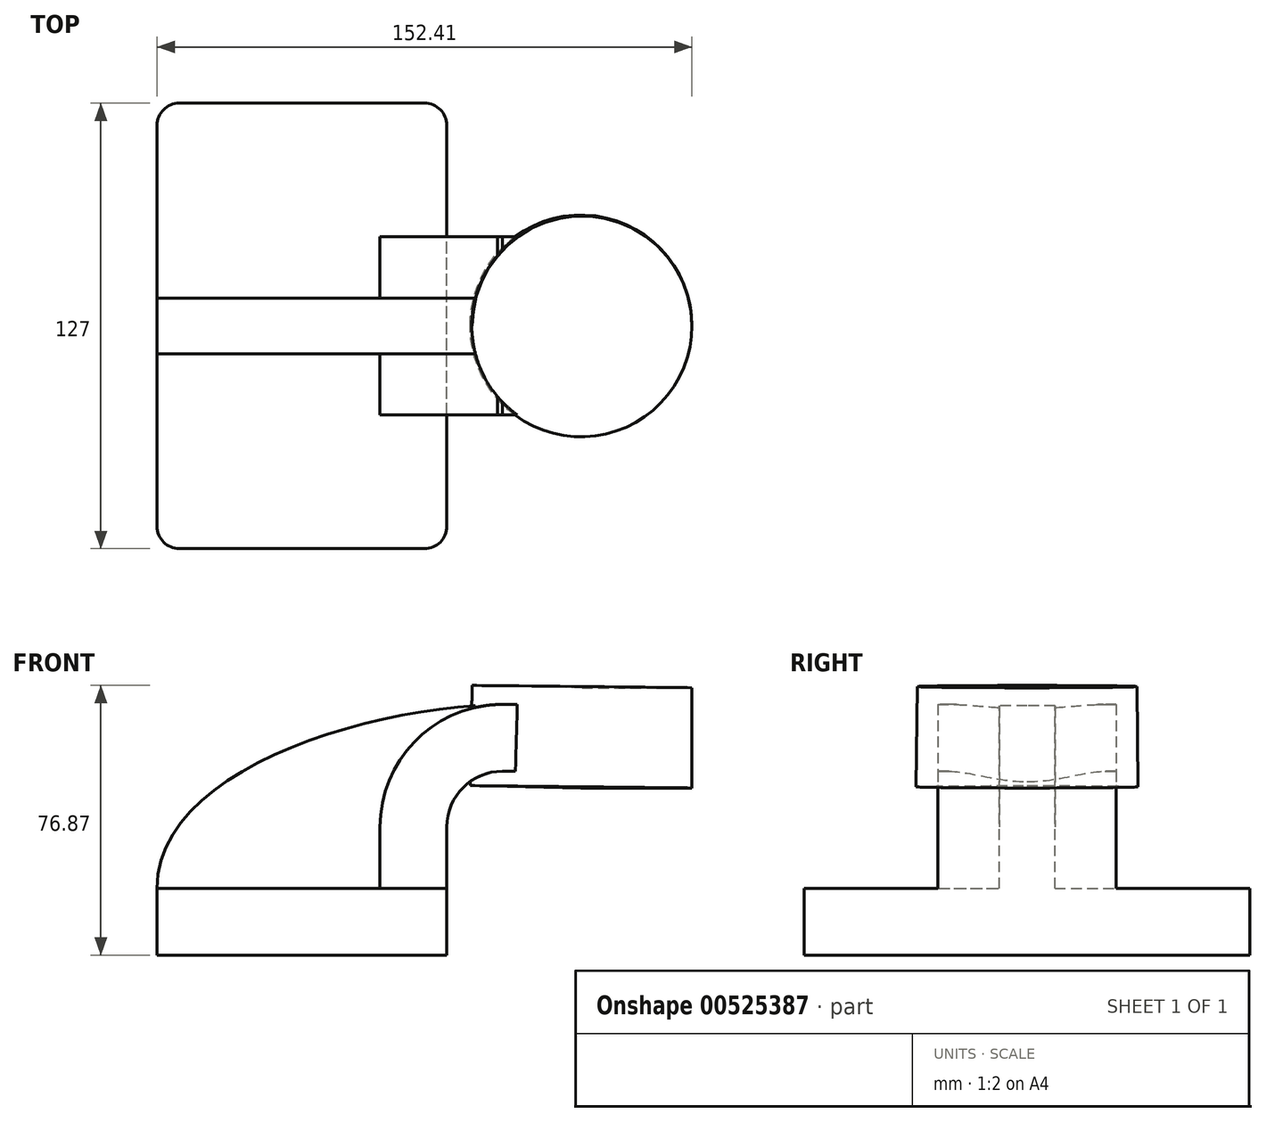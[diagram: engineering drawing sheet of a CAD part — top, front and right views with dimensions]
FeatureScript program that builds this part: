
annotation { "Feature Type Name" : "Feature", "Feature Type Description" : "" }
export const myFeature = defineFeature(function(context is Context, id is Id, definition is map)
    precondition{}
    {
        {
            var Q0;
            Q0=qCreatedBy(makeId("Front.planeOp"),FACE);
            var sketch = newSketch(context, id + "F0", { "sketchPlane" : qUnion([Q0])});
            skLineSegment(sketch, "E0.bottom", {"start": v(-41.27, -9.53) * mm, "end": v(41.28, -9.53) * mm});
            skLineSegment(sketch, "E0.top", {"start": v(-41.28, 9.53) * mm, "end": v(41.28, 9.53) * mm});
            skLineSegment(sketch, "E0.left", {"start": v(-41.28, -9.53) * mm, "end": v(-41.28, 9.53) * mm});
            skLineSegment(sketch, "E0.right", {"start": v(41.28, -9.53) * mm, "end": v(41.28, 9.53) * mm});
            skPoint(sketch, "E0.middle", {"position": v(0, 0) * mm});
            skLineSegment(sketch, "E1.bottom", {"start": v(60.32, 38.1) * mm, "end": v(111.12, 38.1) * mm});
            skLineSegment(sketch, "E1.top", {"start": v(60.32, 66.68) * mm, "end": v(111.12, 66.68) * mm});
            skLineSegment(sketch, "E1.left", {"start": v(60.32, 38.1) * mm, "end": v(60.32, 66.68) * mm});
            skLineSegment(sketch, "E1.right", {"start": v(111.12, 38.1) * mm, "end": v(111.12, 66.68) * mm});
            skPoint(sketch, "E1.middle", {"position": v(85.72, 52.39) * mm});
            skLineSegment(sketch, "E2", {"start": v(41.28, 9.53) * mm, "end": v(41.28, 27) * mm});
            skArc(sketch, "E3", {"start": v(41.27, 27) * mm, "mid": v(45.92, 38.23) * mm, "end": v(57.15, 42.88) * mm});
            skLineSegment(sketch, "E4", {"start": v(57.15, 42.88) * mm, "end": v(79.82, 42.88) * mm});
            skLineSegment(sketch, "E5.0", {"start": v(57.15, 61.93) * mm, "end": v(79.82, 61.93) * mm});
            skArc(sketch, "E5.1", {"start": v(22.22, 27) * mm, "mid": v(32.45, 51.7) * mm, "end": v(57.15, 61.93) * mm});
            skLineSegment(sketch, "E5.2", {"start": v(22.23, 9.53) * mm, "end": v(22.23, 27) * mm});
            skLineSegment(sketch, "E6", {"start": v(79.51, 38.1) * mm, "end": v(79.82, 66.68) * mm});
            skFitSpline(sketch, "E7", {"points": [v(-41.28, 9.53) * mm, v(57.15, 61.93) * mm], "startDerivative": vector(-0.46, 101.4) * mm, "endDerivative": vector(114.73, 1.75) * mm});
            skSolve(sketch);
        }
        {
            var Q0;
            Q0=makeQuery(id+"F0.imprint","IMPRINT",FACE,{"disambiguationData":[TD([[makeQuery(id+"F0.imprint","IMPRINT",EDGE,{"derivedFrom":sQuery(id+"F0.wireOp",EDGE,"E0.bottom")}),1.0]])]});
            extrude(context, id + "F1", {"entities" : qUnion([Q0]), "endBound" : BoundingType.SYMMETRIC, "depth" : 127 * mm, "offsetDistance" : 25.4 * mm});
        }
        {
            var Q0;
            {var subQ0=sQuery(id+"F0.wireOp",EDGE,"E4");var subQ1=sQuery(id+"F0.wireOp",EDGE,"E1.left");var subQ2=makeQuery(id+"F0.imprint","INTERSECT",VERTEX,{"derivedFrom":[subQ1,subQ0]});Q0=makeQuery(id+"F0.imprint","IMPRINT",FACE,{"disambiguationData":[TD([[makeQuery(id+"F0.imprint","IMPRINT",EDGE,{"disambiguationData":[TD([[subQ2,-1.0]])],"derivedFrom":subQ1}),-1.0]])]});}
            var Q1;
            {var subQ1=sQuery(id+"F0.wireOp",EDGE,"E2");Q1=makeQuery(id+"F0.imprint","IMPRINT",FACE,{"disambiguationData":[TD([[makeQuery(id+"F0.imprint","IMPRINT",EDGE,{"derivedFrom":subQ1}),1.0]])]});}
            extrude(context, id + "F2", {"entities" : qUnion([Q0, Q1]), "operationType" : NewBodyOperationType.ADD, "endBound" : BoundingType.SYMMETRIC, "depth" : 50.8 * mm, "offsetDistance" : 25.4 * mm});
        }
        {
            var Q0;
            {var subQ3=sQuery(id+"F0.wireOp",EDGE,"E5.2");Q0=makeQuery(id+"F0.imprint","IMPRINT",FACE,{"disambiguationData":[TD([[makeQuery(id+"F0.imprint","IMPRINT",EDGE,{"derivedFrom":subQ3}),1.0]])]});}
            extrude(context, id + "F3", {"entities" : qUnion([Q0]), "operationType" : NewBodyOperationType.ADD, "endBound" : BoundingType.SYMMETRIC, "depth" : 15.88 * mm, "offsetDistance" : 25.4 * mm});
        }
        {
            var Q0;
            {var subQ4=sQuery(id+"F0.wireOp",EDGE,"E1.right");Q0=makeQuery(id+"F0.imprint","IMPRINT",FACE,{"disambiguationData":[TD([[makeQuery(id+"F0.imprint","IMPRINT",EDGE,{"derivedFrom":subQ4}),1.0]])]});}
            var Q1;
            Q1=sQuery(id+"F0.wireOp",EDGE,"E6");
            revolve(context, id + "F4", {"operationType" : NewBodyOperationType.ADD, "entities" : qUnion([Q0]), "axis" : qUnion([Q1]), "revolveType" : RevolveType.FULL});
        }
        {
            var Q0;
            Q0=makeQuery(id+"F1.opExtrude","CAP_EDGE",EDGE,{"disambiguationData":[OSD([sQuery(id+"F0.wireOp",EDGE,"E0.right")])],"isStart":false});
            var Q1;
            Q1=makeQuery(id+"F1.opExtrude","CAP_EDGE",EDGE,{"disambiguationData":[OSD([sQuery(id+"F0.wireOp",EDGE,"E0.left")])],"isStart":false});
            var Q2;
            Q2=makeQuery(id+"F1.opExtrude","CAP_EDGE",EDGE,{"disambiguationData":[OSD([sQuery(id+"F0.wireOp",EDGE,"E0.left")])],"isStart":true});
            var Q3;
            Q3=makeQuery(id+"F1.opExtrude","CAP_EDGE",EDGE,{"disambiguationData":[OSD([sQuery(id+"F0.wireOp",EDGE,"E0.right")])],"isStart":true});
            fillet(context, id + "F5", {"entities" : qUnion([Q0, Q1, Q2, Q3]), "radius" : 6.35 * mm, "tangentPropagation" : true, "allowEdgeOverflow" : false});
        }
    });
